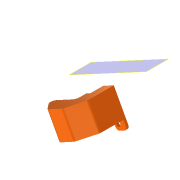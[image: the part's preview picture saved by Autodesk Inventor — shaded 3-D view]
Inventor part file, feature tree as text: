
AUTODESK INVENTOR PART (.ipt)
format: ipt  version: 2022 (Build 260153000, 153)  size: 274,944 bytes
history: native  units: in
note: dims shown in document units (in); Inventor stores cm internally (conversion verified against a paired STEP export)
features: other x8, extrude x7, sketch x6, reference x5, projected_geometry x2, plane x1, fillet x1
ambient origin geometry x8: Origin, YZ Plane, XZ Plane, XY Plane, X Axis, Y Axis, Z Axis, Center Point
bodies: Solid1 (feature_tree)
feature tree (30):
  plane  "Work Plane1"
  extrude  "Extrusion1"  Depth=0.5512in TaperAngle=0.0deg
  extrude  "Extrusion2"  Depth=0.0591in
  extrude  "Extrusion3"  TaperAngle=135.0deg  [1 undecoded]
  extrude  "Extrusion8"  Depth=0.2362in
  extrude  "Extrusion9"  Depth=0.2362in
  extrude  "Extrusion11"  Depth=0.5512in TaperAngle=0.0deg
  extrude  "Extrusion12"  Depth=0.0591in
  fillet  "Rundung1"  Radius=0.0591in
  sketch  "Sketch2"  dims[d0=0.0591in d1=0.0in d3=0.5512in d4=0.0in]
  sketch  "Sketch3"  dims[d12=0.0591in d13=0.0in d22=0.5307in]
  reference  "Reference1"
  projected_geometry  "Projected Loop5"
  projected_geometry  "Projected Loop6"
  sketch  "Sketch8"  dims[d23=0.2653in d25=135.0deg]
  reference  "Reference2"
  reference  "Reference3"
  sketch  "Sketch9"  dims[d26=0.1575in d27=0.2362in]
  reference  "Reference4"
  sketch  "Skizze11"  dims[d28=0.1568in d29=0.2362in]
  sketch  "Skizze12"  dims[d31=0.3937in d35=0.5512in d36=0.0in d40=0.0591in d41=0.0591in d42=0.9449in d43=0.5512in d44=0.0in d45=0.0in d48=0.0in d49=0.0in d50=0.1969in d51=0.3937in d52=0.0in d53=0.0787in]
  reference  "Referenz5"
  other  "<userpath>\Documents\Matchboxscope\INVENTOR\Matchboxscope_v0.iam"
  other  "Matchboxscope_v0.iam"
  other  "Matchboxscope_sample_v0:1"
  other  "Matchboxscope_middle2_v1:1"
  other  "00_ESP3-CAM:5"
  other  "Bauteil50"
  other  "Assembly_Matchboxscope_injectionmolded.iam"
  other  "IM_Matchboxscope_plate:2"
note: 1 required parameter value undecoded (feature->parameter linkage not recoverable at this tier; creation-order binding heuristic only, values carry confidence <= 0.55)
